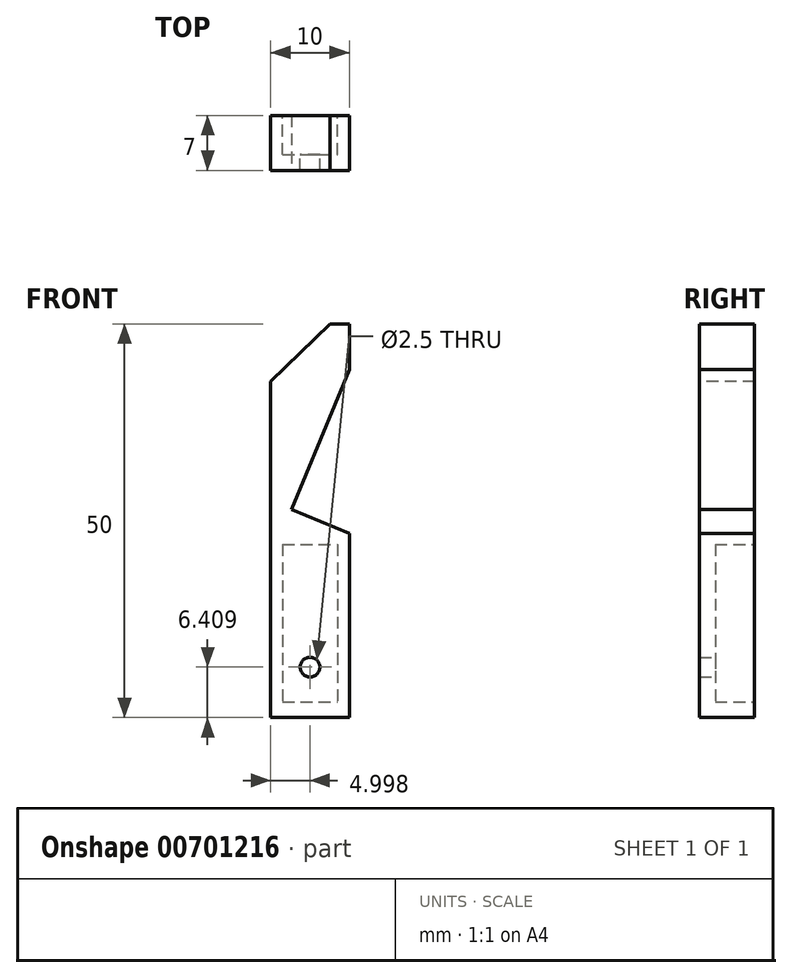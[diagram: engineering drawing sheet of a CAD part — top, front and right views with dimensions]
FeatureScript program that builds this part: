
annotation { "Feature Type Name" : "Feature", "Feature Type Description" : "" }
export const myFeature = defineFeature(function(context is Context, id is Id, definition is map)
    precondition{}
    {
        {
            var Q0;
            Q0=qCreatedBy(makeId("Front.planeOp"),FACE);
            var sketch = newSketch(context, id + "F0", { "sketchPlane" : qUnion([Q0])});
            skLineSegment(sketch, "E0.bottom", {"start": v(-32.17, 52.44) * mm, "end": v(-22.17, 52.44) * mm});
            skLineSegment(sketch, "E0.top", {"start": v(-32.17, 2.44) * mm, "end": v(-22.17, 2.44) * mm});
            skLineSegment(sketch, "E0.left", {"start": v(-32.17, 52.44) * mm, "end": v(-32.17, 2.44) * mm});
            skLineSegment(sketch, "E0.right", {"start": v(-22.17, 52.44) * mm, "end": v(-22.17, 2.44) * mm});
            skSolve(sketch);
        }
        {
            var Q0;
            Q0=qSketchRegion(id+"F0",true);
            extrude(context, id + "F1", {"entities" : qUnion([Q0]), "depth" : 7 * mm, "offsetDistance" : 25 * mm});
        }
        {
            var Q0;
            Q0=makeQuery(id+"F1.opExtrude","CAP_FACE",FACE,{"disambiguationData":[OSD([sQuery(id+"F0.wireOp",EDGE,"E0.bottom"),sQuery(id+"F0.wireOp",EDGE,"E0.top"),sQuery(id+"F0.wireOp",EDGE,"E0.left"),sQuery(id+"F0.wireOp",EDGE,"E0.right")])],"isStart":true});
            var sketch = newSketch(context, id + "F2", { "sketchPlane" : qUnion([Q0])});
            skLineSegment(sketch, "E1.bottom", {"start": v(30.67, 24.44) * mm, "end": v(23.67, 24.44) * mm});
            skLineSegment(sketch, "E1.top", {"start": v(30.67, 4.44) * mm, "end": v(23.67, 4.44) * mm});
            skLineSegment(sketch, "E1.left", {"start": v(30.67, 24.44) * mm, "end": v(30.67, 4.44) * mm});
            skLineSegment(sketch, "E1.right", {"start": v(23.67, 24.44) * mm, "end": v(23.67, 4.44) * mm});
            skSolve(sketch);
        }
        {
            var Q0;
            Q0=qSketchRegion(id+"F2",true);
            extrude(context, id + "F3", {"entities" : qUnion([Q0]), "operationType" : NewBodyOperationType.REMOVE, "oppositeDirection" : true, "depth" : 5 * mm, "offsetDistance" : 25 * mm});
        }
        {
            var Q0;
            Q0=makeQuery(id+"F3.boolean.opBoolean","COPY",FACE,{"derivedFrom":makeQuery(id+"F3.opExtrude","CAP_FACE",FACE,{"disambiguationData":[OSD([sQuery(id+"F2.wireOp",EDGE,"E1.bottom"),sQuery(id+"F2.wireOp",EDGE,"E1.top"),sQuery(id+"F2.wireOp",EDGE,"E1.left"),sQuery(id+"F2.wireOp",EDGE,"E1.right")])],"isStart":false})});
            var sketch = newSketch(context, id + "F4", { "sketchPlane" : qUnion([Q0])});
            skCircle(sketch, "E2", {"center": v(27.17, 8.85) * mm, "radius": 1.25 * mm});
            skSolve(sketch);
        }
        {
            var Q0;
            Q0=qSketchRegion(id+"F4",true);
            extrude(context, id + "F5", {"entities" : qUnion([Q0]), "operationType" : NewBodyOperationType.REMOVE, "endBound" : BoundingType.THROUGH_ALL, "oppositeDirection" : true, "depth" : 25 * mm, "offsetDistance" : 25 * mm});
        }
        {
            var Q0;
            Q0=makeQuery(id+"F1.opExtrude","CAP_FACE",FACE,{"disambiguationData":[OSD([sQuery(id+"F0.wireOp",EDGE,"E0.bottom"),sQuery(id+"F0.wireOp",EDGE,"E0.top"),sQuery(id+"F0.wireOp",EDGE,"E0.left"),sQuery(id+"F0.wireOp",EDGE,"E0.right")])],"isStart":false});
            var sketch = newSketch(context, id + "F6", { "sketchPlane" : qUnion([Q0])});
            skLineSegment(sketch, "E3", {"start": v(-32.17, 45.14) * mm, "end": v(-24.65, 52.44) * mm});
            skLineSegment(sketch, "E4", {"start": v(-32.17, 45.14) * mm, "end": v(-32.17, 52.44) * mm});
            skLineSegment(sketch, "E5", {"start": v(-32.17, 52.44) * mm, "end": v(-24.65, 52.44) * mm});
            skLineSegment(sketch, "E6", {"start": v(-22.17, 25.82) * mm, "end": v(-29.55, 28.89) * mm});
            skLineSegment(sketch, "E7", {"start": v(-29.55, 28.89) * mm, "end": v(-22.17, 46.65) * mm});
            skLineSegment(sketch, "E8", {"start": v(-22.17, 46.65) * mm, "end": v(-22.17, 25.82) * mm});
            skPoint(sketch, "E9", {"position": v(-22.17, 27.44) * mm});
            skSolve(sketch);
        }
        {
            var Q0;
            Q0=qSketchRegion(id+"F6",true);
            extrude(context, id + "F7", {"entities" : qUnion([Q0]), "operationType" : NewBodyOperationType.REMOVE, "endBound" : BoundingType.THROUGH_ALL, "oppositeDirection" : true, "depth" : 25 * mm, "offsetDistance" : 25 * mm});
        }
    });
